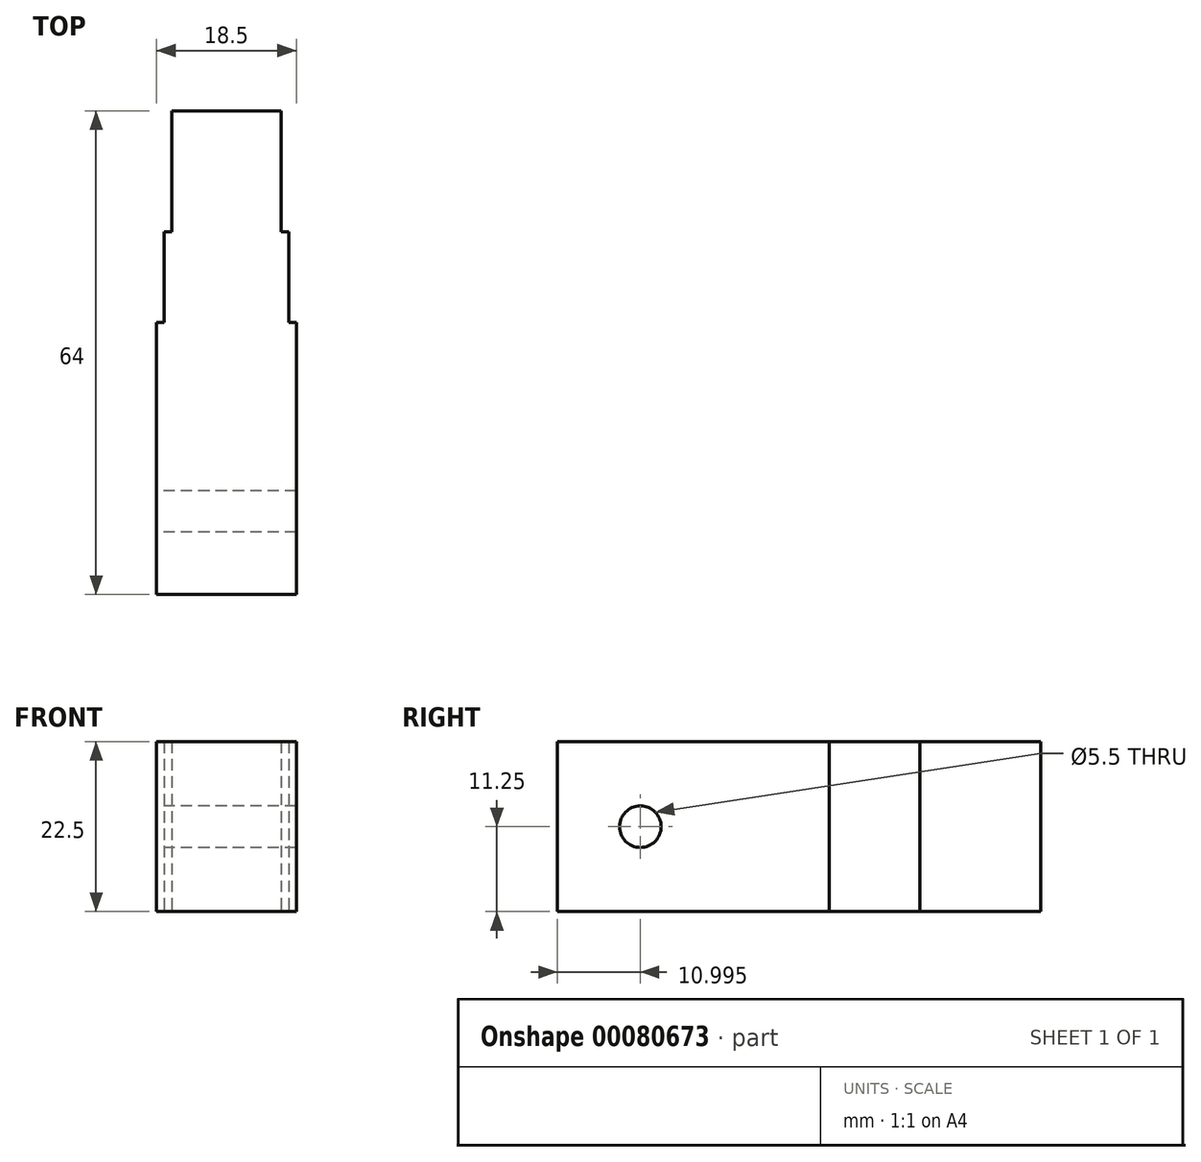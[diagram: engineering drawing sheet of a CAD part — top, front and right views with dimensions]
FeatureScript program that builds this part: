
annotation { "Feature Type Name" : "Feature", "Feature Type Description" : "" }
export const myFeature = defineFeature(function(context is Context, id is Id, definition is map)
    precondition{}
    {
        {
            var Q0;
            Q0=qCreatedBy(makeId("Top.planeOp"),FACE);
            var sketch = newSketch(context, id + "F0", { "sketchPlane" : qUnion([Q0])});
            skLineSegment(sketch, "E0.bottom", {"start": v(0, -13.12) * mm, "end": v(9.25, -13.12) * mm});
            skLineSegment(sketch, "E0.top", {"start": v(0, 50.88) * mm, "end": v(7.25, 50.88) * mm});
            skLineSegment(sketch, "E0.left", {"start": v(0, -13.12) * mm, "end": v(0, 50.88) * mm});
            skLineSegment(sketch, "E0.right", {"start": v(9.25, -13.12) * mm, "end": v(9.25, 22.88) * mm});
            skLineSegment(sketch, "E1", {"start": v(7.25, 50.88) * mm, "end": v(7.25, 34.88) * mm});
            skLineSegment(sketch, "E2", {"start": v(7.25, 34.88) * mm, "end": v(8.25, 34.88) * mm});
            skLineSegment(sketch, "E3", {"start": v(8.25, 34.88) * mm, "end": v(8.25, 22.88) * mm});
            skLineSegment(sketch, "E4", {"start": v(8.25, 22.88) * mm, "end": v(9.25, 22.88) * mm});
            skLineSegment(sketch, "E5.MirrorCS", {"start": v(0, 50.88) * mm, "end": v(-7.25, 50.88) * mm});
            skLineSegment(sketch, "E6.MirrorCS", {"start": v(-7.25, 50.88) * mm, "end": v(-7.25, 34.88) * mm});
            skLineSegment(sketch, "E7.MirrorCS", {"start": v(-7.25, 34.88) * mm, "end": v(-8.25, 34.88) * mm});
            skLineSegment(sketch, "E8.MirrorCS", {"start": v(-8.25, 34.88) * mm, "end": v(-8.25, 22.88) * mm});
            skLineSegment(sketch, "E9.MirrorCS", {"start": v(-8.25, 22.88) * mm, "end": v(-9.25, 22.88) * mm});
            skLineSegment(sketch, "E10.MirrorCS", {"start": v(-9.25, -13.12) * mm, "end": v(-9.25, 22.88) * mm});
            skLineSegment(sketch, "E11.MirrorCS", {"start": v(0, -13.12) * mm, "end": v(-9.25, -13.12) * mm});
            skSolve(sketch);
        }
        {
            var Q0;
            {var subQ1=sQuery(id+"F0.wireOp",EDGE,"E0.bottom");Q0=makeQuery(id+"F0.imprint","IMPRINT",FACE,{"disambiguationData":[TD([[makeQuery(id+"F0.imprint","IMPRINT",EDGE,{"derivedFrom":subQ1}),1.0]])]});}
            var Q1;
            Q1=makeQuery(id+"F0.imprint","IMPRINT",FACE,{"disambiguationData":[TD([[makeQuery(id+"F0.imprint","IMPRINT",EDGE,{"derivedFrom":sQuery(id+"F0.wireOp",EDGE,"E0.left")}),1.0]])]});
            extrude(context, id + "F1", {"entities" : qUnion([Q0, Q1]), "depth" : 22.5 * mm});
        }
        {
            var Q0;
            Q0=makeQuery(id+"F1.opExtrude","SWEPT_FACE",FACE,{"disambiguationData":[OSD([sQuery(id+"F0.wireOp",EDGE,"E10.MirrorCS")])]});
            cPlane(context, id + "F2", {"entities" : qUnion([Q0]), "cplaneType" : CPlaneType.OFFSET, "offset" : 0 * mm, "width" : 150 * mm, "height" : 150 * mm});
        }
        {
            var Q0;
            Q0=qCreatedBy(id+"F2.planeOp",FACE);
            var sketch = newSketch(context, id + "F3", { "sketchPlane" : qUnion([Q0])});
            skLineSegment(sketch, "E12", {"start": v(2.12, 0) * mm, "end": v(2.12, 22.5) * mm, "construction": true});
            skLineSegment(sketch, "E13", {"start": v(2.12, 11.25) * mm, "end": v(-18.12, 11.25) * mm, "construction": true});
            skPoint(sketch, "E13.endSnap0", {"position": v(2.12, 11.25) * mm});
            skCircle(sketch, "E14", {"center": v(2.12, 11.25) * mm, "radius": 2.75 * mm});
            skSolve(sketch);
        }
        {
            var Q0;
            Q0 = qSketchRegion(id + "F3", true);
            extrude(context, id + "F4", {"entities" : qUnion([Q0]), "operationType" : NewBodyOperationType.REMOVE, "oppositeDirection" : true, "depth" : 22.5 * mm});
        }
    });
